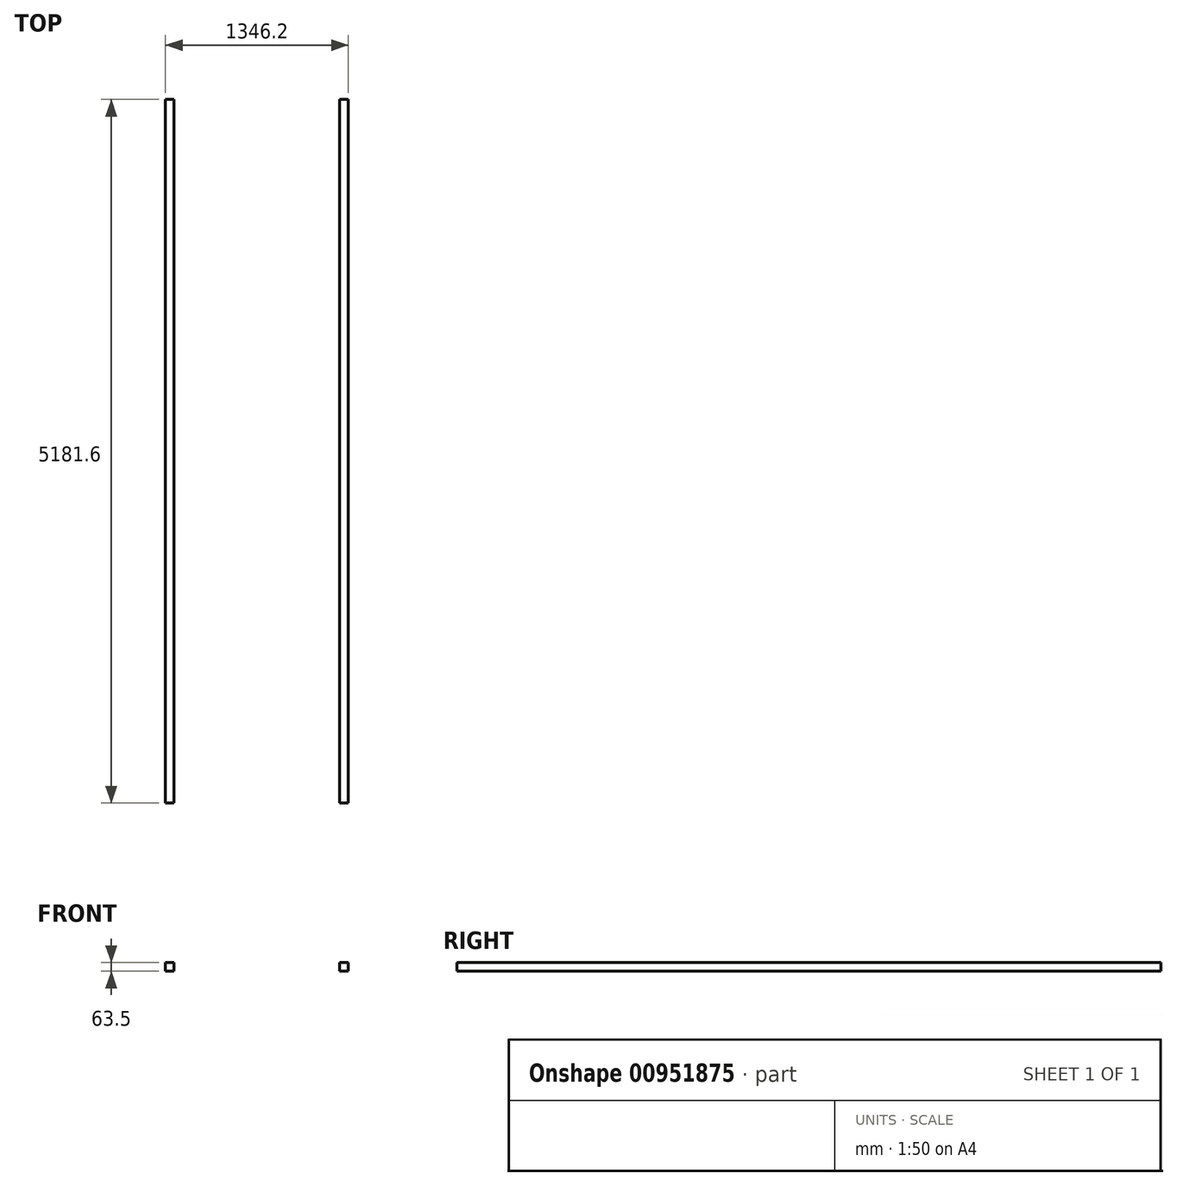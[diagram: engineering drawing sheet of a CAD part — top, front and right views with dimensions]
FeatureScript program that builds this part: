
annotation { "Feature Type Name" : "Feature", "Feature Type Description" : "" }
export const myFeature = defineFeature(function(context is Context, id is Id, definition is map)
    precondition{}
    {
        {
            var Q0;
            Q0=qCreatedBy(makeId("Top.planeOp"),FACE);
            var sketch = newSketch(context, id + "F0", { "sketchPlane" : qUnion([Q0])});
            skLineSegment(sketch, "E0", {"start": v(-673.1, 2589.75) * mm, "end": v(-673.1, -2591.85) * mm});
            skLineSegment(sketch, "E1", {"start": v(-673.1, 2589.75) * mm, "end": v(-609.6, 2589.75) * mm});
            skLineSegment(sketch, "E2", {"start": v(-609.6, 2589.75) * mm, "end": v(-609.6, -2591.85) * mm});
            skLineSegment(sketch, "E3", {"start": v(-609.6, -2591.85) * mm, "end": v(-673.1, -2591.85) * mm});
            skLineSegment(sketch, "E4.MirrorCS", {"start": v(609.6, 2589.75) * mm, "end": v(609.6, -2591.85) * mm});
            skLineSegment(sketch, "E5.MirrorCS", {"start": v(673.1, 2589.75) * mm, "end": v(673.1, -2591.85) * mm});
            skLineSegment(sketch, "E6", {"start": v(609.6, 2589.75) * mm, "end": v(673.1, 2589.75) * mm});
            skLineSegment(sketch, "E7", {"start": v(-609.6, 2589.75) * mm, "end": v(-673.1, 2589.75) * mm});
            skLineSegment(sketch, "E8", {"start": v(673.1, -2591.85) * mm, "end": v(609.6, -2591.85) * mm});
            skLineSegment(sketch, "E9", {"start": v(-609.6, -2591.85) * mm, "end": v(609.6, -2591.85) * mm});
            skLineSegment(sketch, "E10", {"start": v(609.6, -1657.66) * mm, "end": v(-609.6, -1657.66) * mm});
            skLineSegment(sketch, "E11", {"start": v(609.6, -746.97) * mm, "end": v(-609.6, -746.97) * mm});
            skLineSegment(sketch, "E12.MirrorCS", {"start": v(609.6, 746.97) * mm, "end": v(-609.6, 746.97) * mm});
            skLineSegment(sketch, "E13.MirrorCS", {"start": v(609.6, 1657.66) * mm, "end": v(-609.6, 1657.66) * mm});
            skLineSegment(sketch, "E14", {"start": v(609.6, 2589.75) * mm, "end": v(-609.6, 2589.75) * mm});
            skSolve(sketch);
        }
        {
            var Q0;
            Q0=makeQuery(id+"F0.imprint","IMPRINT",FACE,{"disambiguationData":[TD([[makeQuery(id+"F0.imprint","IMPRINT",EDGE,{"derivedFrom":sQuery(id+"F0.wireOp",EDGE,"E4.MirrorCS")}),1.0]])]});
            var Q1;
            Q1=makeQuery(id+"F0.imprint","IMPRINT",FACE,{"disambiguationData":[TD([[makeQuery(id+"F0.imprint","IMPRINT",EDGE,{"derivedFrom":sQuery(id+"F0.wireOp",EDGE,"E0")}),1.0]])]});
            extrude(context, id + "F1", {"entities" : qUnion([Q0, Q1]), "depth" : 63.5 * mm, "offsetDistance" : 25.4 * mm});
        }
    });
